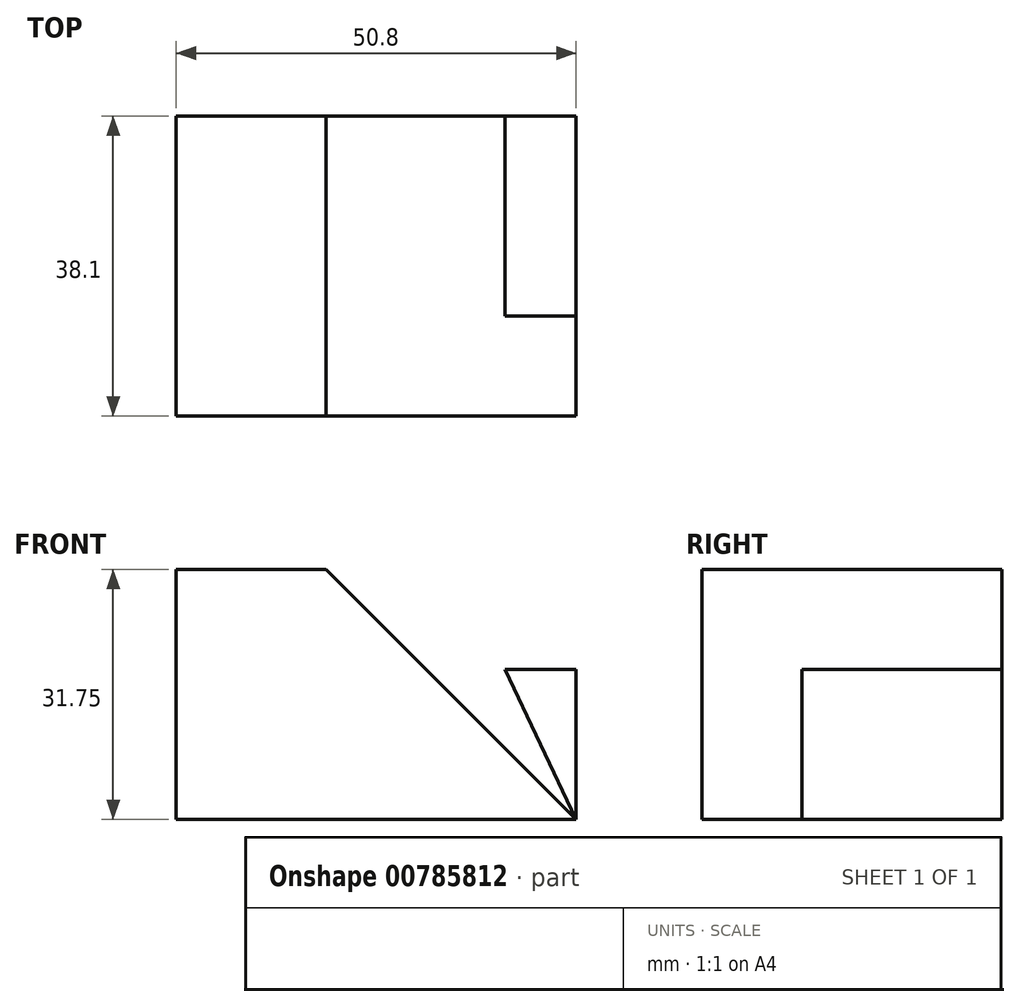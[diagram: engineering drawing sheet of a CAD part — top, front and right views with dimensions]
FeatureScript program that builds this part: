
annotation { "Feature Type Name" : "Feature", "Feature Type Description" : "" }
export const myFeature = defineFeature(function(context is Context, id is Id, definition is map)
    precondition{}
    {
        {
            var Q0;
            Q0=qCreatedBy(makeId("Front.planeOp"),FACE);
            var sketch = newSketch(context, id + "F0", { "sketchPlane" : qUnion([Q0])});
            skLineSegment(sketch, "E0", {"start": v(0, 0) * mm, "end": v(25.4, 0) * mm});
            skLineSegment(sketch, "E1", {"start": v(25.4, 0) * mm, "end": v(25.4, 31.75) * mm});
            skLineSegment(sketch, "E2", {"start": v(-25.4, 31.75) * mm, "end": v(25.4, 31.75) * mm});
            skLineSegment(sketch, "E3", {"start": v(-25.4, 31.75) * mm, "end": v(-25.4, 0) * mm});
            skLineSegment(sketch, "E4", {"start": v(0, 0) * mm, "end": v(-25.4, 0) * mm});
            skSolve(sketch);
        }
        {
            var Q0;
            Q0=makeQuery(id+"F0.imprint","IMPRINT",FACE,{"disambiguationData":[TD([[makeQuery(id+"F0.imprint","IMPRINT",EDGE,{"derivedFrom":sQuery(id+"F0.wireOp",EDGE,"E0")}),1.0]])]});
            extrude(context, id + "F1", {"entities" : qUnion([Q0]), "depth" : 38.1 * mm, "offsetDistance" : 25.4 * mm});
        }
        {
            var Q0;
            Q0=makeQuery(id+"F1.opExtrude","CAP_FACE",FACE,{"disambiguationData":[OSD([sQuery(id+"F0.wireOp",EDGE,"E0"),sQuery(id+"F0.wireOp",EDGE,"E1"),sQuery(id+"F0.wireOp",EDGE,"E2"),sQuery(id+"F0.wireOp",EDGE,"E3"),sQuery(id+"F0.wireOp",EDGE,"E4")])],"isStart":false});
            var sketch = newSketch(context, id + "F2", { "sketchPlane" : qUnion([Q0])});
            skLineSegment(sketch, "E5", {"start": v(-25.4, 31.75) * mm, "end": v(-6.35, 31.75) * mm});
            skLineSegment(sketch, "E6", {"start": v(25.4, 0) * mm, "end": v(-6.35, 31.75) * mm});
            skSolve(sketch);
        }
        {
            var Q0;
            {var subQ0=sQuery(id+"F2.wireOp",EDGE,"E6");Q0=makeQuery(id+"F2.imprint","IMPRINT",FACE,{"disambiguationData":[TD([[makeQuery(id+"F2.imprint","IMPRINT",EDGE,{"derivedFrom":subQ0}),-1.0]])]});}
            extrude(context, id + "F3", {"entities" : qUnion([Q0]), "operationType" : NewBodyOperationType.REMOVE, "oppositeDirection" : true, "depth" : 12.7 * mm, "offsetDistance" : 25.4 * mm});
        }
        {
            var Q0;
            Q0=makeQuery(id+"F3.boolean.opBoolean","COPY",FACE,{"derivedFrom":makeQuery(id+"F3.opExtrude","CAP_FACE",FACE,{"disambiguationData":[OSD([sQuery(id+"F0.wireOp",EDGE,"E1"),sQuery(id+"F0.wireOp",EDGE,"E2"),sQuery(id+"F2.wireOp",EDGE,"E6")])],"isStart":false})});
            var sketch = newSketch(context, id + "F4", { "sketchPlane" : qUnion([Q0])});
            skLineSegment(sketch, "E7", {"start": v(25.4, 31.75) * mm, "end": v(10.4, 31.75) * mm});
            skLineSegment(sketch, "E8", {"start": v(10.4, 31.75) * mm, "end": v(25.4, 0) * mm});
            skSolve(sketch);
        }
        {
            var Q0;
            {var subQ0=sQuery(id+"F4.wireOp",EDGE,"E8");Q0=makeQuery(id+"F4.imprint","IMPRINT",FACE,{"disambiguationData":[TD([[makeQuery(id+"F4.imprint","IMPRINT",EDGE,{"derivedFrom":subQ0}),-1.0]])]});}
            extrude(context, id + "F5", {"entities" : qUnion([Q0]), "operationType" : NewBodyOperationType.REMOVE, "oppositeDirection" : true, "depth" : 25.4 * mm, "offsetDistance" : 25.4 * mm});
        }
        {
            var Q0;
            {var subQ0=sQuery(id+"F0.wireOp",EDGE,"E2");var subQ1=sQuery(id+"F0.wireOp",EDGE,"E1");Q0=makeQuery(id+"F5.boolean.opBoolean","SPLIT",FACE,{"disambiguationData":[TD([makeQuery(id+"F1.opExtrude","SWEPT_FACE",FACE,{"disambiguationData":[OSD([subQ1])]})])],"derivedFrom":makeQuery(id+"F1.opExtrude","SWEPT_FACE",FACE,{"disambiguationData":[OSD([subQ0])]})});}
            extrude(context, id + "F6", {"entities" : qUnion([Q0]), "operationType" : NewBodyOperationType.REMOVE, "oppositeDirection" : true, "depth" : 12.7 * mm, "offsetDistance" : 25.4 * mm});
        }
    });
